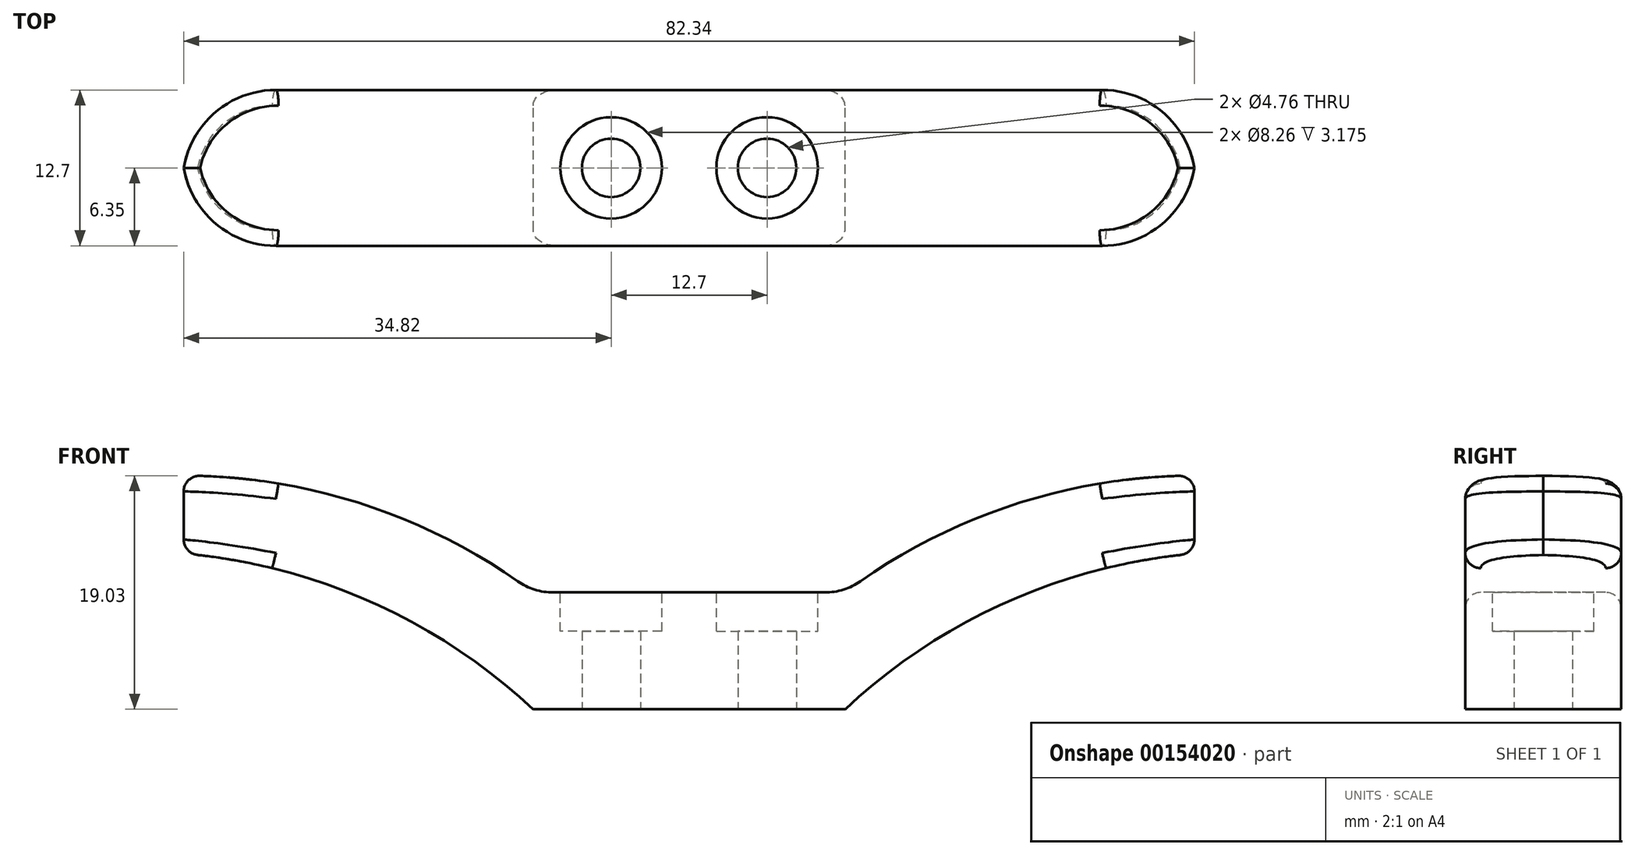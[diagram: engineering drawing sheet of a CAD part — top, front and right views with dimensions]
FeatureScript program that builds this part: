
annotation { "Feature Type Name" : "Feature", "Feature Type Description" : "" }
export const myFeature = defineFeature(function(context is Context, id is Id, definition is map)
    precondition{}
    {
        {
            var Q0;
            Q0=qCreatedBy(makeId("Front.planeOp"),FACE);
            var sketch = newSketch(context, id + "F0", { "sketchPlane" : qUnion([Q0])});
            skLineSegment(sketch, "E0.bottom", {"start": v(0, 0) * mm, "end": v(-41.28, 0) * mm, "construction": true});
            skLineSegment(sketch, "E0.top", {"start": v(0, 19.05) * mm, "end": v(-41.28, 19.05) * mm, "construction": true});
            skLineSegment(sketch, "E0.left", {"start": v(0, 0) * mm, "end": v(0, 19.05) * mm, "construction": true});
            skLineSegment(sketch, "E0.right", {"start": v(-41.28, 0) * mm, "end": v(-41.28, 19.05) * mm, "construction": true});
            skLineSegment(sketch, "E1.bottom", {"start": v(0, 0) * mm, "end": v(-12.7, 0) * mm});
            skLineSegment(sketch, "E1.top", {"start": v(0, 9.53) * mm, "end": v(-12.7, 9.53) * mm});
            skLineSegment(sketch, "E1.left", {"start": v(0, 0) * mm, "end": v(0, 9.52) * mm});
            skLineSegment(sketch, "E1.right", {"start": v(-12.7, 0) * mm, "end": v(-12.7, 9.52) * mm});
            skLineSegment(sketch, "E2", {"start": v(-41.28, 19.05) * mm, "end": v(-41.28, 12.7) * mm});
            skArc(sketch, "E3", {"start": v(-12.7, 0) * mm, "mid": v(-25.92, 8.76) * mm, "end": v(-41.28, 12.7) * mm});
            skArc(sketch, "E4", {"start": v(-12.7, 9.53) * mm, "mid": v(-26.21, 16.6) * mm, "end": v(-41.28, 19.05) * mm});
            skSolve(sketch);
        }
        {
            var Q0;
            Q0=makeQuery(id+"F0.imprint","IMPRINT",FACE,{"disambiguationData":[TD([[makeQuery(id+"F0.imprint","IMPRINT",EDGE,{"derivedFrom":sQuery(id+"F0.wireOp",EDGE,"E1.right")}),1.0]])]});
            var Q1;
            Q1=makeQuery(id+"F0.imprint","IMPRINT",FACE,{"disambiguationData":[TD([[makeQuery(id+"F0.imprint","IMPRINT",EDGE,{"derivedFrom":sQuery(id+"F0.wireOp",EDGE,"E1.bottom")}),-1.0]])]});
            extrude(context, id + "F1", {"entities" : qUnion([Q0, Q1]), "endBound" : BoundingType.SYMMETRIC, "depth" : 12.7 * mm});
        }
        {
            var Q0;
            Q0=qCreatedBy(makeId("Top.planeOp"),FACE);
            var sketch = newSketch(context, id + "F2", { "sketchPlane" : qUnion([Q0])});
            skLineSegment(sketch, "E5", {"start": v(0, 0) * mm, "end": v(-47.4, 0) * mm});
            skCircle(sketch, "E6", {"center": v(-6.35, 0) * mm, "radius": 2.38 * mm});
            skCircle(sketch, "E7", {"center": v(-6.35, 0) * mm, "radius": 3.18 * mm, "construction": true});
            skSolve(sketch);
        }
        {
            var Q0;
            {var subQ0=sQuery(id+"F2.wireOp",EDGE,"E6");var subQ1=sQuery(id+"F2.wireOp",EDGE,"E5");var subQ2=makeQuery(id+"F2.imprint","INTERSECT",VERTEX,{"disambiguationData":[OD(0.0)],"derivedFrom":[subQ1,subQ0]});Q0=makeQuery(id+"F2.imprint","IMPRINT",FACE,{"disambiguationData":[TD([[makeQuery(id+"F2.imprint","IMPRINT",EDGE,{"disambiguationData":[TD([[subQ2,1.0]])],"derivedFrom":subQ1}),1.0]])]});}
            var Q1;
            Q1 = qSketchRegion(id + "F2", true);
            extrude(context, id + "F3", {"entities" : qUnion([Q0, Q1]), "operationType" : NewBodyOperationType.REMOVE, "endBound" : BoundingType.THROUGH_ALL, "depth" : 25.4 * mm});
        }
        {
            var Q0;
            Q0=makeQuery(id+"F1.opExtrude","SWEPT_FACE",FACE,{"disambiguationData":[OSD([sQuery(id+"F0.wireOp",EDGE,"E1.top")])]});
            var sketch = newSketch(context, id + "F4", { "sketchPlane" : qUnion([Q0])});
            skCircle(sketch, "E8", {"center": v(-6.35, 0) * mm, "radius": 4.13 * mm});
            skSolve(sketch);
        }
        {
            var Q0;
            Q0=makeQuery(id+"F4.imprint","IMPRINT",FACE,{"disambiguationData":[TD([[makeQuery(id+"F4.imprint","IMPRINT",EDGE,{"derivedFrom":sQuery(id+"F4.wireOp",EDGE,"E8")}),1.0]])]});
            extrude(context, id + "F5", {"entities" : qUnion([Q0]), "operationType" : NewBodyOperationType.REMOVE, "oppositeDirection" : true, "depth" : 3.17 * mm});
        }
        {
            var Q0;
            Q0=makeQuery(id+"F1.opExtrude","CAP_EDGE",EDGE,{"disambiguationData":[OSD([sQuery(id+"F0.wireOp",EDGE,"E2")])],"isStart":false});
            var Q1;
            Q1=makeQuery(id+"F1.opExtrude","CAP_EDGE",EDGE,{"disambiguationData":[OSD([sQuery(id+"F0.wireOp",EDGE,"E2")])],"isStart":true});
            fillet(context, id + "F6", {"entities" : qUnion([Q0, Q1]), "radius" : 7.62 * mm, "tangentPropagation" : true, "allowEdgeOverflow" : false});
        }
        {
            var Q0;
            Q0=makeQuery(id+"F1.opExtrude","SWEPT_EDGE",EDGE,{"disambiguationData":[OSD([sQuery(id+"F0.wireOp",EDGE,"E1.top"),sQuery(id+"F0.wireOp",EDGE,"E1.right"),sQuery(id+"F0.wireOp",EDGE,"E4")])]});
            fillet(context, id + "F7", {"entities" : qUnion([Q0]), "radius" : 5.08 * mm, "tangentPropagation" : true, "allowEdgeOverflow" : false});
        }
        {
            var Q0;
            Q0=makeQuery(id+"F1.opExtrude","CAP_EDGE",EDGE,{"disambiguationData":[OSD([sQuery(id+"F0.wireOp",EDGE,"E3")])],"isStart":false});
            var Q1;
            Q1=makeQuery(id+"F6.opFillet","BLEND_EDGE",EDGE,{"blendedFrom":[makeQuery(id+"F1.opExtrude","CAP_EDGE",EDGE,{"disambiguationData":[OSD([sQuery(id+"F0.wireOp",EDGE,"E2")])],"isStart":false}),makeQuery(id+"F1.opExtrude","SWEPT_FACE",FACE,{"disambiguationData":[OSD([sQuery(id+"F0.wireOp",EDGE,"E3")])]})],"blendedInto":[makeQuery(id+"F1.opExtrude","SWEPT_FACE",FACE,{"disambiguationData":[OSD([sQuery(id+"F0.wireOp",EDGE,"E3")])]})]});
            var Q2;
            Q2=makeQuery(id+"F1.opExtrude","CAP_EDGE",EDGE,{"disambiguationData":[OSD([sQuery(id+"F0.wireOp",EDGE,"E4")])],"isStart":false});
            var Q3;
            Q3=makeQuery(id+"F6.opFillet","BLEND_EDGE",EDGE,{"blendedFrom":[makeQuery(id+"F1.opExtrude","CAP_EDGE",EDGE,{"disambiguationData":[OSD([sQuery(id+"F0.wireOp",EDGE,"E2")])],"isStart":false}),makeQuery(id+"F1.opExtrude","SWEPT_FACE",FACE,{"disambiguationData":[OSD([sQuery(id+"F0.wireOp",EDGE,"E4")])]})],"blendedInto":[makeQuery(id+"F1.opExtrude","SWEPT_FACE",FACE,{"disambiguationData":[OSD([sQuery(id+"F0.wireOp",EDGE,"E4")])]})]});
            var Q4;
            Q4=makeQuery(id+"F1.opExtrude","CAP_EDGE",EDGE,{"disambiguationData":[OSD([sQuery(id+"F0.wireOp",EDGE,"E3")])],"isStart":true});
            var Q5;
            Q5=makeQuery(id+"F6.opFillet","BLEND_EDGE",EDGE,{"blendedFrom":[makeQuery(id+"F1.opExtrude","CAP_EDGE",EDGE,{"disambiguationData":[OSD([sQuery(id+"F0.wireOp",EDGE,"E2")])],"isStart":true}),makeQuery(id+"F1.opExtrude","SWEPT_FACE",FACE,{"disambiguationData":[OSD([sQuery(id+"F0.wireOp",EDGE,"E3")])]})],"blendedInto":[makeQuery(id+"F1.opExtrude","SWEPT_FACE",FACE,{"disambiguationData":[OSD([sQuery(id+"F0.wireOp",EDGE,"E3")])]})]});
            var Q6;
            Q6=makeQuery(id+"F6.opFillet","BLEND_EDGE",EDGE,{"blendedFrom":[makeQuery(id+"F1.opExtrude","CAP_EDGE",EDGE,{"disambiguationData":[OSD([sQuery(id+"F0.wireOp",EDGE,"E2")])],"isStart":true}),makeQuery(id+"F1.opExtrude","SWEPT_FACE",FACE,{"disambiguationData":[OSD([sQuery(id+"F0.wireOp",EDGE,"E4")])]})],"blendedInto":[makeQuery(id+"F1.opExtrude","SWEPT_FACE",FACE,{"disambiguationData":[OSD([sQuery(id+"F0.wireOp",EDGE,"E4")])]})]});
            var Q7;
            Q7=makeQuery(id+"F1.opExtrude","CAP_EDGE",EDGE,{"disambiguationData":[OSD([sQuery(id+"F0.wireOp",EDGE,"E4")])],"isStart":true});
            var Q8;
            Q8=makeQuery(id+"F1.opExtrude","CAP_EDGE",EDGE,{"disambiguationData":[OSD([sQuery(id+"F0.wireOp",EDGE,"E1.top")])],"isStart":false});
            var Q9;
            Q9=makeQuery(id+"F1.opExtrude","CAP_EDGE",EDGE,{"disambiguationData":[OSD([sQuery(id+"F0.wireOp",EDGE,"E1.top")])],"isStart":true});
            fillet(context, id + "F8", {"entities" : qUnion([Q0, Q1, Q2, Q3, Q4, Q5, Q6, Q7, Q8, Q9]), "radius" : 1.27 * mm, "allowEdgeOverflow" : false});
        }
        {
            var Q0;
            Q0=makeQuery(id+"F1.opExtrude","SWEPT_BODY",BODY,{"disambiguationData":[OSD([sQuery(id+"F0.wireOp",EDGE,"E1.bottom"),sQuery(id+"F0.wireOp",EDGE,"E1.top"),sQuery(id+"F0.wireOp",EDGE,"E1.left"),sQuery(id+"F0.wireOp",EDGE,"E2"),sQuery(id+"F0.wireOp",EDGE,"E3"),sQuery(id+"F0.wireOp",EDGE,"E4")])]});
            var Q1;
            Q1=qCreatedBy(makeId("Right.planeOp"),FACE);
            mirror(context, id + "F9", {"operationType" : NewBodyOperationType.ADD, "entities" : qUnion([Q0]), "mirrorPlane" : qUnion([Q1])});
        }
    });
